# Revit family: Hager-VEGA-Surface_mounted-IP40-With_Cover-With_DIN-Hosted-BE-fr
name_source: partatom
category: Electrical Equipment
units: mm (PartAtom-declared; Revit-internal decimal feet)

## family parameters
Cut with Voids When Loaded = No
Host = Face
Maintain Annotation Orientation = Yes
Panel Configuration = Two Columns, Circuits Across
Part Type = Panelboard
Room Calculation Point = No
Round Connector Dimension = Use Diameter
Shared = No

## types (10) — shared parameters
BC_MODEL_ID = 1546981
BC_OBJECT_ID = 513427
BC_OBJECT_VERSION = #5
Code hager = ADD-EC000214_EU
EF000003 - Type de montage = Apparent
EF000008 - Largeur = 400 mm  [stored 1.31234 ft]
EF000024 - Résistant aux UV = No
EF000049 - Profondeur = 146 mm  [stored 0.479003 ft]
EF000116 - Numéro RAL = 9010
EF001062 - Finition CEM = No
EF001134 - Avec Rail DIN = Yes
EF002950 - Largeur dans les unités de partition = 18
EF005474 - Classe de protection (IP) = IP40
EF006306 - Avec serrure = No
EF015777 - Borne à conducteur neutre = No
ETIM class code = EC000214
ETIM class name = Small distribution board
HG000001-nombre de colonnes = 1
HG000002-avec porte = Yes
HG000003-Gamme = VEGA
HG000005-Epaisseur = 2 mm  [stored 0.00656168 ft]
HG000006-Encastré = No
HG000009-Porte à double battant = No
HG000010-Portes asymétriques = No
HG000012-Angle de pivotement de la porte = 90.00°
HG000013-Porte à gauche = No
HG000014-Porte à droite = Yes
HG000015-Visibilité de l'emprise de la porte = Yes
HG000016-Visibilité de la porte 3D = Yes
HG000017-Distance entre pôles = 18 mm  [stored 0.0590551 ft]
HG000060-RAL-number = 9010
HG000099-ID modèle Onfly = 507532
HGEF0002950-largeur en nombre de modules = 18
Manufacturer = Hager
Name = VEGA-Surface_mounted-IP40-With_Cover-With_DIN-BE
Name BIM&CO = Electricity
Name hager = ADD_Enclosures_EC000214
Uniformat = Low Tension Service & Dist.
Uniformat code = D501001
zero-valued in all types: Default Elevation, EF000218 - Profondeur d'encastrement, EF000332 - Hauteur d'encastrement, EF000846 - Largeur de montage, EF001131 - Profondeur intérieure, HG000007-Nombre de colonnes vides

## per-type parameters (varying)
| type | BC_VARIANT_ID | EF000007 - Couleur | EF000040 - Hauteur | EF000118 - Avec plaque de montage | EF000266 - Nombre de rangées | EF001088 - Possibilité de montage en saillie | EF004462 - Type de fermeture | EF006244 - Couvercle/porte transparent(e) | EF009212 - Finition du couvercle | EF015776 - Borne de mise à la terre | EF015941 - Porte pour transmission du signal | HG000004-Référence fabricant | HG000008-Nombre de rangées vides | HG000011-Rangées du bas vides | HGEF000266-Nombre de rangées |
| VEGA-Surface_mounted_W400_H325_D146_18_Modular_Spacing-VB118B | 1173838 | Blanc | 325 mm  [stored 1.06627 ft] | No | 1 | Yes | Autre | No | Fermé | Yes | Yes | VB118B | 0 | No | 1 |
| VEGA-Surface_mounted_W400_H325_D146_18_Modular_Spacing-VB118R | 1173839 |  | 325 mm  [stored 1.06627 ft] | No | 1 | No |  | No |  | No | No | VB118R | 0 | No | 1 |
| VEGA-Surface_mounted_W400_H475_D146_18_Modular_Spacing-VB218B | 1173840 | Blanc | 475 mm  [stored 1.5584 ft] | No | 2 | Yes | Autre | No | Fermé | Yes | Yes | VB218B | 0 | No | 2 |
| VEGA-Surface_mounted_W400_H475_D146_18_Modular_Spacing-VB218R | 1173841 |  | 475 mm  [stored 1.5584 ft] | No | 2 | No |  | No |  | No | No | VB218R | 0 | No | 2 |
| VEGA-Surface_mounted_W400_H625_D146_18_Modular_Spacing-VB318B | 1173842 | Blanc | 625 mm  [stored 2.05052 ft] | No | 3 | Yes | Autre | No | Fermé | Yes | Yes | VB318B | 0 | No | 3 |
| VEGA-Surface_mounted_W400_H625_D146_18_Modular_Spacing-VB318MMT | 1173843 | Blanc | 625 mm  [stored 2.05052 ft] | Yes | 3 | Yes | Autre | Yes | Avec échancrure | No | Yes | VB318MMT | 2 | Yes | 3 |
| VEGA-Surface_mounted_W400_H625_D146_18_Modular_Spacing-VB318R | 1173844 |  | 625 mm  [stored 2.05052 ft] | No | 3 | No |  | No |  | No | No | VB318R | 0 | No | 3 |
| VEGA-Surface_mounted_W400_H775_D146_18_Modular_Spacing-VB418B | 1173845 | Blanc | 775 mm  [stored 2.54265 ft] | No | 4 | Yes | Autre | No | Fermé | Yes | Yes | VB418B | 0 | No | 4 |
| VEGA-Surface_mounted_W400_H775_D146_18_Modular_Spacing-VB418MMT | 1173846 | Blanc | 775 mm  [stored 2.54265 ft] | Yes | 4 | Yes | Autre | Yes | Avec échancrure | No | Yes | VB418MMT | 3 | Yes | 4 |
| VEGA-Surface_mounted_W400_H775_D146_18_Modular_Spacing-VB418R | 1173847 |  | 775 mm  [stored 2.54265 ft] | No | 4 | No |  | No |  | No | No | VB418R | 0 | No | 4 |

note: column(s) folded — value = type name in every type: Reference

note: [stored X ft] marks values corroborated as IEEE doubles in the binary element streams (Revit-internal decimal feet)

## geometry (parser evidence)
native form markers: Sweep x14
no freeform markers — native parametric forms only
